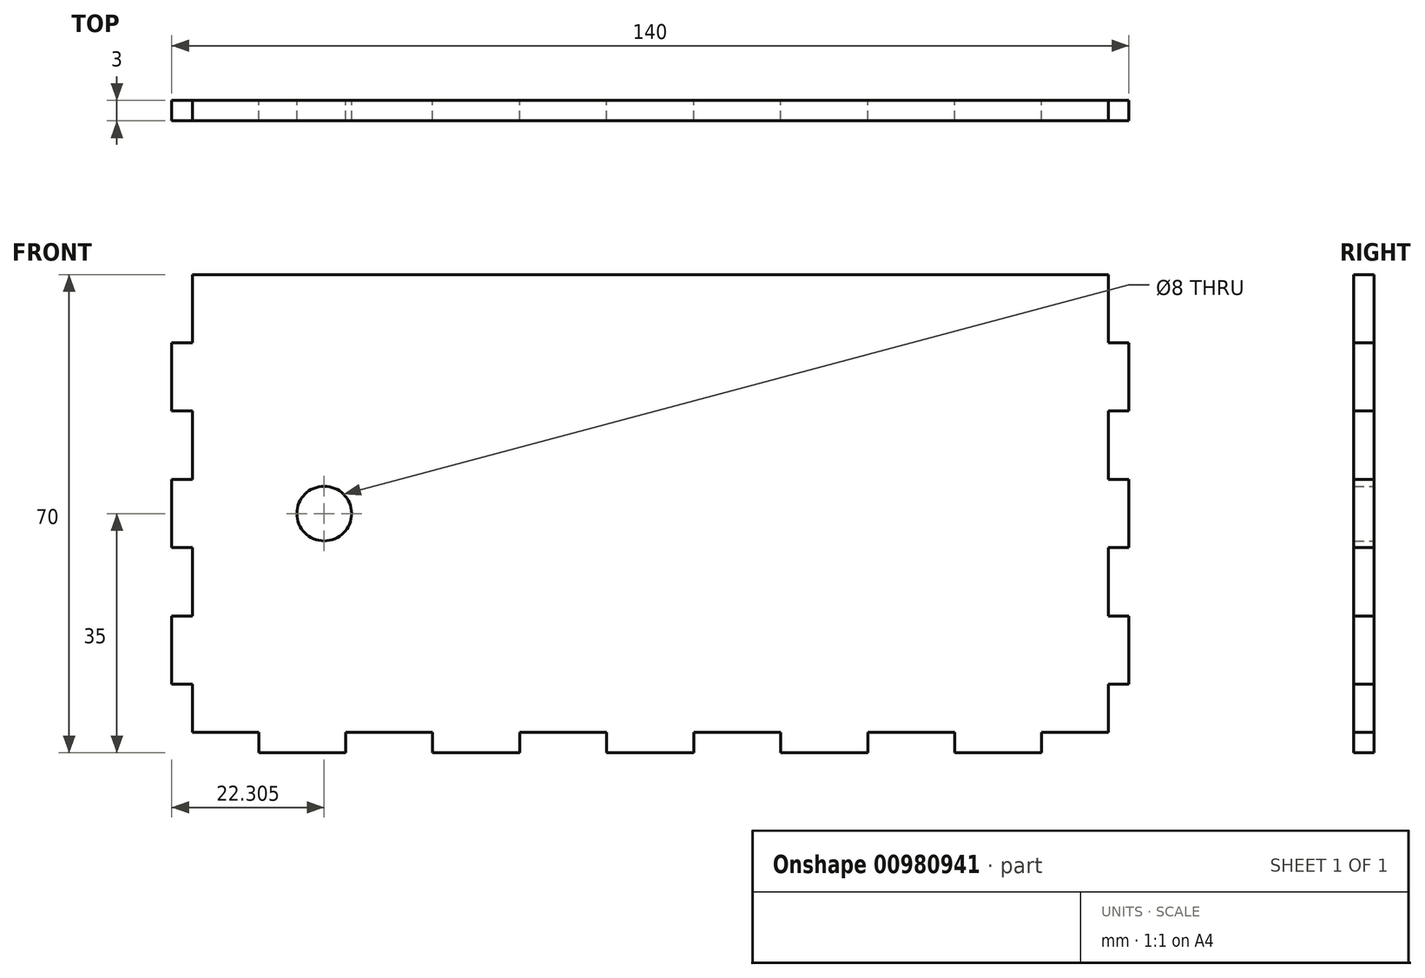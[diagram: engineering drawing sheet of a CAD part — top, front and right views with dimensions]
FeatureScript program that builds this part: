
annotation { "Feature Type Name" : "Feature", "Feature Type Description" : "" }
export const myFeature = defineFeature(function(context is Context, id is Id, definition is map)
    precondition{}
    {
        {
            var Q0;
            Q0=qCreatedBy(makeId("Front.planeOp"),FACE);
            var sketch = newSketch(context, id + "F0", { "sketchPlane" : qUnion([Q0])});
            skLineSegment(sketch, "E0.top", {"start": v(67, 35) * mm, "end": v(-67, 35) * mm});
            skPoint(sketch, "E0.middle", {"position": v(0, 0) * mm});
            skLineSegment(sketch, "E1", {"start": v(-67, -32) * mm, "end": v(-57.27, -32) * mm});
            skLineSegment(sketch, "E2", {"start": v(-57.27, -32) * mm, "end": v(-57.27, -35) * mm});
            skLineSegment(sketch, "E3", {"start": v(-57.27, -35) * mm, "end": v(-44.55, -35) * mm});
            skLineSegment(sketch, "E4", {"start": v(-44.55, -35) * mm, "end": v(-44.55, -32) * mm});
            skLineSegment(sketch, "E5", {"start": v(-44.55, -32) * mm, "end": v(-31.82, -32) * mm});
            skLineSegment(sketch, "E6.1.0.0", {"start": v(-19.1, -32) * mm, "end": v(-6.36, -32) * mm});
            skLineSegment(sketch, "E6.1.0.1", {"start": v(-31.82, -35) * mm, "end": v(-19.1, -35) * mm});
            skLineSegment(sketch, "E6.1.0.3", {"start": v(-19.1, -35) * mm, "end": v(-19.1, -32) * mm});
            skLineSegment(sketch, "E6.1.0.4", {"start": v(-31.82, -32) * mm, "end": v(-31.82, -35) * mm});
            skLineSegment(sketch, "E6.2.0.0", {"start": v(6.36, -32) * mm, "end": v(19.1, -32) * mm});
            skLineSegment(sketch, "E6.2.0.1", {"start": v(-6.36, -35) * mm, "end": v(6.36, -35) * mm});
            skLineSegment(sketch, "E6.2.0.2", {"start": v(-19.1, -32) * mm, "end": v(-6.36, -32) * mm});
            skLineSegment(sketch, "E6.2.0.3", {"start": v(6.36, -35) * mm, "end": v(6.36, -32) * mm});
            skLineSegment(sketch, "E6.2.0.4", {"start": v(-6.36, -32) * mm, "end": v(-6.36, -35) * mm});
            skLineSegment(sketch, "E6.3.0.0", {"start": v(31.82, -32) * mm, "end": v(44.55, -32) * mm});
            skLineSegment(sketch, "E6.3.0.1", {"start": v(19.1, -35) * mm, "end": v(31.82, -35) * mm});
            skLineSegment(sketch, "E6.3.0.2", {"start": v(6.36, -32) * mm, "end": v(19.1, -32) * mm});
            skLineSegment(sketch, "E6.3.0.3", {"start": v(31.82, -35) * mm, "end": v(31.82, -32) * mm});
            skLineSegment(sketch, "E6.3.0.4", {"start": v(19.1, -32) * mm, "end": v(19.1, -35) * mm});
            skLineSegment(sketch, "E6.4.0.0", {"start": v(57.27, -32) * mm, "end": v(67, -32) * mm});
            skLineSegment(sketch, "E6.4.0.1", {"start": v(44.55, -35) * mm, "end": v(57.27, -35) * mm});
            skLineSegment(sketch, "E6.4.0.2", {"start": v(31.82, -32) * mm, "end": v(44.55, -32) * mm});
            skLineSegment(sketch, "E6.4.0.3", {"start": v(57.27, -35) * mm, "end": v(57.27, -32) * mm});
            skLineSegment(sketch, "E6.4.0.4", {"start": v(44.55, -32) * mm, "end": v(44.55, -35) * mm});
            skLineSegment(sketch, "E6.direction1", {"start": v(-67, -32) * mm, "end": v(-44.55, -32) * mm, "construction": true});
            skLineSegment(sketch, "E7", {"start": v(-67, -32) * mm, "end": v(-67, -25) * mm});
            skLineSegment(sketch, "E8", {"start": v(-67, -25) * mm, "end": v(-70, -25) * mm});
            skLineSegment(sketch, "E9", {"start": v(-70, -25) * mm, "end": v(-70, -15) * mm});
            skLineSegment(sketch, "E10", {"start": v(-70, -15) * mm, "end": v(-67, -15) * mm});
            skPoint(sketch, "E0.right.start.orphan", {"position": v(-70, -35) * mm});
            skLineSegment(sketch, "E11.1.0.1", {"start": v(-70, -5) * mm, "end": v(-70, 5) * mm});
            skPoint(sketch, "E11.1.0.3", {"position": v(-70, -15) * mm});
            skLineSegment(sketch, "E11.1.0.4", {"start": v(-70, 5) * mm, "end": v(-67, 5) * mm});
            skLineSegment(sketch, "E11.1.0.5", {"start": v(-67, -5) * mm, "end": v(-70, -5) * mm});
            skLineSegment(sketch, "E11.2.0.1", {"start": v(-70, 15) * mm, "end": v(-70, 25) * mm});
            skLineSegment(sketch, "E11.2.0.2", {"start": v(-67, 25) * mm, "end": v(-67, 35) * mm});
            skPoint(sketch, "E11.2.0.3", {"position": v(-70, 5) * mm});
            skLineSegment(sketch, "E11.2.0.4", {"start": v(-70, 25) * mm, "end": v(-67, 25) * mm});
            skLineSegment(sketch, "E11.2.0.5", {"start": v(-67, 15) * mm, "end": v(-70, 15) * mm});
            skLineSegment(sketch, "E11.direction1", {"start": v(-67, -32) * mm, "end": v(-67, -15) * mm, "construction": true});
            skPoint(sketch, "E12.orphan", {"position": v(-67, -5) * mm});
            skPoint(sketch, "E13.orphan", {"position": v(-67, 15) * mm});
            skLineSegment(sketch, "E14", {"start": v(-67, -15) * mm, "end": v(-67, -5) * mm});
            skLineSegment(sketch, "E15", {"start": v(-67, 5) * mm, "end": v(-67, 15) * mm});
            skPoint(sketch, "E16.orphan", {"position": v(-70, 35) * mm});
            skPoint(sketch, "E17.orphan", {"position": v(-70, -32) * mm});
            skPoint(sketch, "E0.left.start.orphan", {"position": v(70, -35) * mm});
            skLineSegment(sketch, "E18.MirrorCS", {"start": v(67, -32) * mm, "end": v(67, -25) * mm});
            skLineSegment(sketch, "E19.MirrorCS", {"start": v(70, 25) * mm, "end": v(67, 25) * mm});
            skLineSegment(sketch, "E20.MirrorCS", {"start": v(70, -25) * mm, "end": v(70, -15) * mm});
            skPoint(sketch, "E21.MirrorP", {"position": v(70, 5) * mm});
            skPoint(sketch, "E22.MirrorP", {"position": v(70, 35) * mm});
            skLineSegment(sketch, "E23.MirrorCS", {"start": v(70, -15) * mm, "end": v(67, -15) * mm});
            skLineSegment(sketch, "E24.MirrorCS", {"start": v(67, 5) * mm, "end": v(67, 15) * mm});
            skLineSegment(sketch, "E25.MirrorCS", {"start": v(67, 25) * mm, "end": v(67, 35) * mm});
            skLineSegment(sketch, "E26.MirrorCS", {"start": v(70, 15) * mm, "end": v(70, 25) * mm});
            skLineSegment(sketch, "E27.MirrorCS", {"start": v(67, -5) * mm, "end": v(70, -5) * mm});
            skPoint(sketch, "E28.MirrorP", {"position": v(70, -32) * mm});
            skPoint(sketch, "E29.MirrorP", {"position": v(67, 15) * mm});
            skPoint(sketch, "E30.MirrorP", {"position": v(67, -5) * mm});
            skLineSegment(sketch, "E31.MirrorCS", {"start": v(67, -32) * mm, "end": v(67, -15) * mm, "construction": true});
            skLineSegment(sketch, "E32.MirrorCS", {"start": v(70, 5) * mm, "end": v(67, 5) * mm});
            skLineSegment(sketch, "E33.MirrorCS", {"start": v(70, -5) * mm, "end": v(70, 5) * mm});
            skLineSegment(sketch, "E34.MirrorCS", {"start": v(67, 15) * mm, "end": v(70, 15) * mm});
            skPoint(sketch, "E35.MirrorP", {"position": v(70, -15) * mm});
            skLineSegment(sketch, "E36.MirrorCS", {"start": v(67, -15) * mm, "end": v(67, -5) * mm});
            skLineSegment(sketch, "E37.MirrorCS", {"start": v(67, -25) * mm, "end": v(70, -25) * mm});
            skCircle(sketch, "E38", {"center": v(-47.7, 0) * mm, "radius": 4 * mm});
            skSolve(sketch);
        }
        {
            var Q0;
            Q0=makeQuery(id+"F0.imprint","IMPRINT",FACE,{"disambiguationData":[TD([[makeQuery(id+"F0.imprint","IMPRINT",EDGE,{"derivedFrom":sQuery(id+"F0.wireOp",EDGE,"E0.top")}),1.0]])]});
            extrude(context, id + "F1", {"entities" : qUnion([Q0]), "depth" : 3 * mm, "offsetDistance" : 25 * mm});
        }
    });
